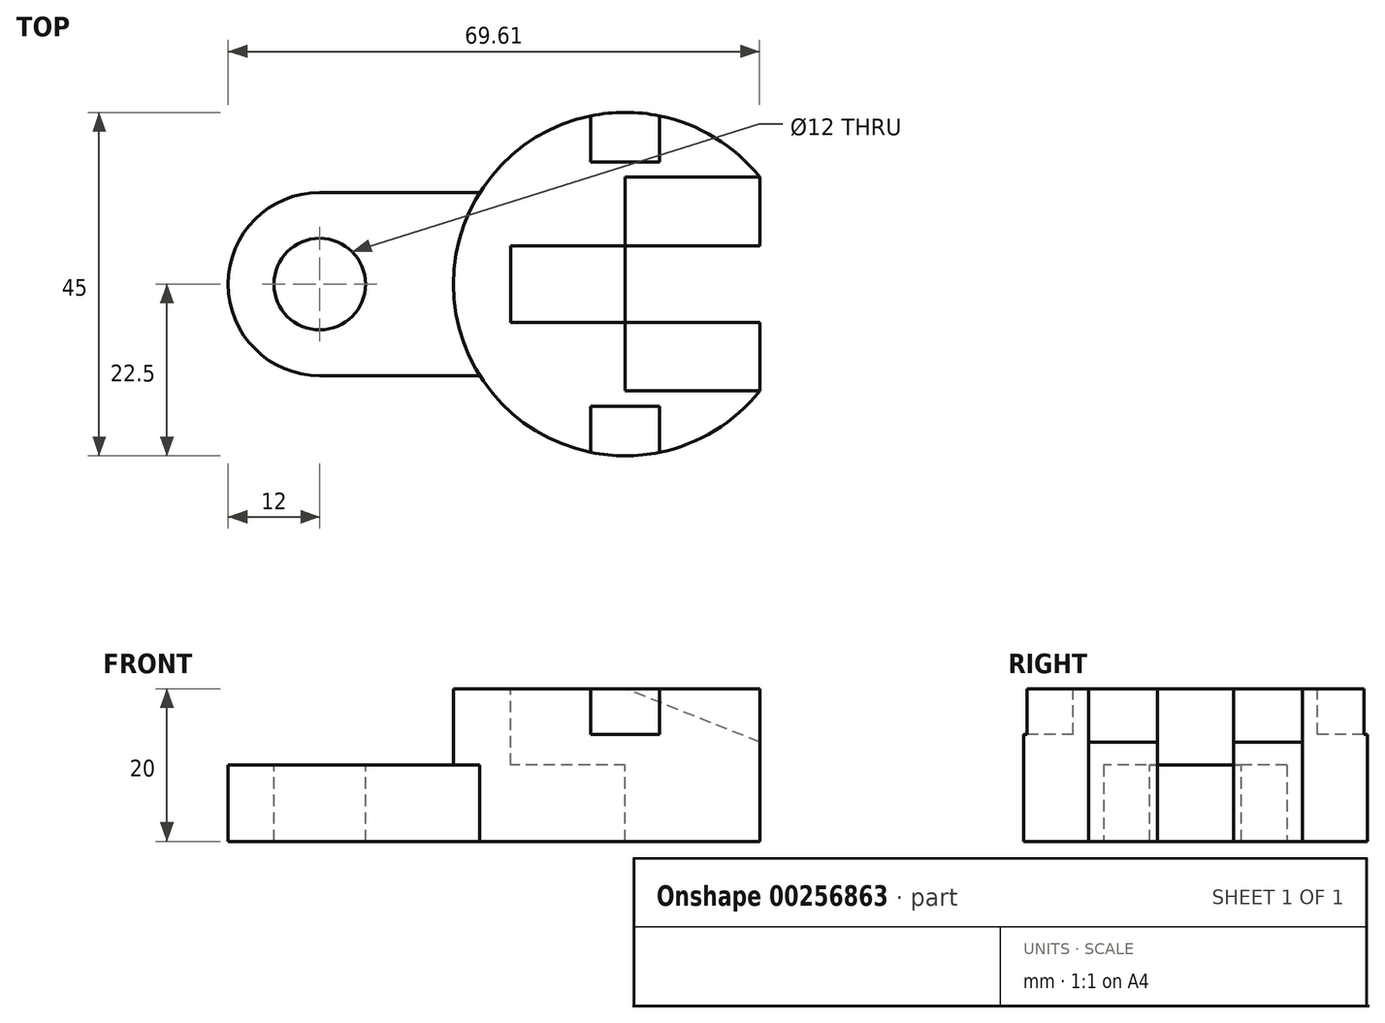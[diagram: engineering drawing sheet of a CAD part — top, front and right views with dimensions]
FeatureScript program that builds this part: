
annotation { "Feature Type Name" : "Feature", "Feature Type Description" : "" }
export const myFeature = defineFeature(function(context is Context, id is Id, definition is map)
    precondition{}
    {
        {
            var Q0;
            Q0=qCreatedBy(makeId("Top.planeOp"),FACE);
            var sketch = newSketch(context, id + "F0", { "sketchPlane" : qUnion([Q0])});
            skCircle(sketch, "E0", {"center": v(0, 0) * mm, "radius": 22.5 * mm});
            skSolve(sketch);
        }
        {
            var Q0;
            Q0=makeQuery(id+"F0.imprint","IMPRINT",FACE,{"disambiguationData":[TD([[makeQuery(id+"F0.imprint","IMPRINT",EDGE,{"derivedFrom":sQuery(id+"F0.wireOp",EDGE,"E0")}),1.0]])]});
            extrude(context, id + "F1", {"entities" : qUnion([Q0]), "endBound" : BoundingType.SYMMETRIC, "depth" : 20 * mm});
        }
        {
            var Q0;
            Q0=makeQuery(id+"F1.opExtrude","CAP_FACE",FACE,{"disambiguationData":[OSD([sQuery(id+"F0.wireOp",EDGE,"E0")])],"isStart":false});
            var sketch = newSketch(context, id + "F2", { "sketchPlane" : qUnion([Q0])});
            skLineSegment(sketch, "E1.bottom", {"start": v(22.5, -22.5) * mm, "end": v(-22.5, -22.5) * mm});
            skLineSegment(sketch, "E1.top", {"start": v(22.5, 22.5) * mm, "end": v(-22.5, 22.5) * mm});
            skLineSegment(sketch, "E1.left", {"start": v(22.5, -22.5) * mm, "end": v(22.5, 22.5) * mm});
            skLineSegment(sketch, "E1.right", {"start": v(-22.5, -22.5) * mm, "end": v(-22.5, 22.5) * mm});
            skPoint(sketch, "E1.middle", {"position": v(0, 0) * mm});
            skLineSegment(sketch, "E2", {"start": v(22.5, 14) * mm, "end": v(-22.5, 14) * mm});
            skLineSegment(sketch, "E3", {"start": v(22.5, -14) * mm, "end": v(-22.5, -14) * mm});
            skLineSegment(sketch, "E4", {"start": v(17.61, 14) * mm, "end": v(17.61, -14) * mm});
            skSolve(sketch);
        }
        {
            var Q0;
            {var subQ0=sQuery(id+"F2.wireOp",EDGE,"E4");Q0=makeQuery(id+"F2.imprint","IMPRINT",FACE,{"disambiguationData":[TD([[makeQuery(id+"F2.imprint","IMPRINT",EDGE,{"derivedFrom":subQ0}),1.0]])]});}
            extrude(context, id + "F3", {"entities" : qUnion([Q0]), "operationType" : NewBodyOperationType.REMOVE, "endBound" : BoundingType.THROUGH_ALL, "oppositeDirection" : true, "depth" : 25 * mm});
        }
        {
            var Q0;
            Q0=makeQuery(id+"F1.opExtrude","CAP_FACE",FACE,{"disambiguationData":[OSD([sQuery(id+"F0.wireOp",EDGE,"E0")])],"isStart":false});
            var sketch = newSketch(context, id + "F4", { "sketchPlane" : qUnion([Q0])});
            skLineSegment(sketch, "E5.bottom", {"start": v(22.5, 22.5) * mm, "end": v(-22.5, 22.5) * mm});
            skLineSegment(sketch, "E5.top", {"start": v(22.5, -22.5) * mm, "end": v(-22.5, -22.5) * mm});
            skLineSegment(sketch, "E5.left", {"start": v(22.5, 22.5) * mm, "end": v(22.5, -22.5) * mm});
            skLineSegment(sketch, "E5.right", {"start": v(-22.5, 22.5) * mm, "end": v(-22.5, -22.5) * mm});
            skPoint(sketch, "E5.middle", {"position": v(0, 0) * mm});
            skLineSegment(sketch, "E6", {"start": v(-22.5, 16) * mm, "end": v(22.5, 16) * mm});
            skLineSegment(sketch, "E7", {"start": v(-22.5, -16) * mm, "end": v(22.5, -16) * mm});
            skLineSegment(sketch, "E8", {"start": v(4.5, 22.05) * mm, "end": v(4.5, -22.05) * mm});
            skLineSegment(sketch, "E9", {"start": v(-4.5, 22.05) * mm, "end": v(-4.5, -22.05) * mm});
            skSolve(sketch);
        }
        {
            var Q0;
            {var subQ4=sQuery(id+"F4.wireOp",EDGE,"E9");var subQ6=sQuery(id+"F4.wireOp",EDGE,"E7");var subQ7=makeQuery(id+"F4.imprint","INTERSECT",VERTEX,{"derivedFrom":[subQ6,subQ4]});Q0=makeQuery(id+"F4.imprint","IMPRINT",FACE,{"disambiguationData":[TD([[makeQuery(id+"F4.imprint","IMPRINT",EDGE,{"disambiguationData":[TD([[subQ7,-1.0]])],"derivedFrom":subQ6}),-1.0]])]});}
            var Q1;
            {var subQ3=sQuery(id+"F4.wireOp",EDGE,"E6");var subQ6=sQuery(id+"F4.wireOp",EDGE,"E9");var subQ8=makeQuery(id+"F4.imprint","INTERSECT",VERTEX,{"derivedFrom":[subQ3,subQ6]});Q1=makeQuery(id+"F4.imprint","IMPRINT",FACE,{"disambiguationData":[TD([[makeQuery(id+"F4.imprint","IMPRINT",EDGE,{"disambiguationData":[TD([[subQ8,-1.0]])],"derivedFrom":subQ3}),1.0]])]});}
            extrude(context, id + "F5", {"entities" : qUnion([Q0, Q1]), "operationType" : NewBodyOperationType.REMOVE, "oppositeDirection" : true, "depth" : 6 * mm});
        }
        {
            var Q0;
            Q0=qCreatedBy(makeId("Front.planeOp"),FACE);
            var sketch = newSketch(context, id + "F6", { "sketchPlane" : qUnion([Q0])});
            skLineSegment(sketch, "E10.bottom", {"start": v(22.5, 10) * mm, "end": v(-22.5, 10) * mm});
            skLineSegment(sketch, "E10.top", {"start": v(22.5, -10) * mm, "end": v(-22.5, -10) * mm});
            skLineSegment(sketch, "E10.left", {"start": v(22.5, 10) * mm, "end": v(22.5, -10) * mm});
            skLineSegment(sketch, "E10.right", {"start": v(-22.5, 10) * mm, "end": v(-22.5, -10) * mm});
            skPoint(sketch, "E10.middle", {"position": v(0, 0) * mm});
            skLineSegment(sketch, "E11", {"start": v(-22.5, 3) * mm, "end": v(22.5, 3) * mm});
            skPoint(sketch, "E12.endSnap0", {"position": v(0, -10) * mm});
            skPoint(sketch, "E13", {"position": v(17.61, 3) * mm});
            skLineSegment(sketch, "E14", {"start": v(0, 10) * mm, "end": v(17.61, 3) * mm});
            skLineSegment(sketch, "E15", {"start": v(17.61, 3) * mm, "end": v(17.61, 10) * mm});
            skSolve(sketch);
        }
        {
            var Q0;
            {var subQ0=sQuery(id+"F6.wireOp",EDGE,"E14");Q0=makeQuery(id+"F6.imprint","IMPRINT",FACE,{"disambiguationData":[TD([[makeQuery(id+"F6.imprint","IMPRINT",EDGE,{"derivedFrom":subQ0}),1.0]])]});}
            extrude(context, id + "F7", {"entities" : qUnion([Q0]), "operationType" : NewBodyOperationType.REMOVE, "endBound" : BoundingType.SYMMETRIC, "oppositeDirection" : true, "depth" : 28 * mm});
        }
        {
            var Q0;
            Q0=qCreatedBy(makeId("Top.planeOp"),FACE);
            var sketch = newSketch(context, id + "F8", { "sketchPlane" : qUnion([Q0])});
            skLineSegment(sketch, "E16.bottom", {"start": v(22.5, 22.5) * mm, "end": v(-22.5, 22.5) * mm});
            skLineSegment(sketch, "E16.top", {"start": v(22.5, -22.5) * mm, "end": v(-22.5, -22.5) * mm});
            skLineSegment(sketch, "E16.left", {"start": v(22.5, 22.5) * mm, "end": v(22.5, -22.5) * mm});
            skLineSegment(sketch, "E16.right", {"start": v(-22.5, 22.5) * mm, "end": v(-22.5, -22.5) * mm});
            skPoint(sketch, "E16.middle", {"position": v(0, 0) * mm});
            skLineSegment(sketch, "E17", {"start": v(-22.5, 5) * mm, "end": v(22.5, 5) * mm});
            skLineSegment(sketch, "E18", {"start": v(-22.5, -5) * mm, "end": v(22.5, -5) * mm});
            skLineSegment(sketch, "E19", {"start": v(-15, 22.5) * mm, "end": v(-15, -22.5) * mm});
            skSolve(sketch);
        }
        {
            var Q0;
            {var subQ0=sQuery(id+"F8.wireOp",EDGE,"E17");var subQ1=sQuery(id+"F8.wireOp",EDGE,"E16.left");var subQ2=makeQuery(id+"F8.imprint","INTERSECT",VERTEX,{"derivedFrom":[subQ1,subQ0]});Q0=makeQuery(id+"F8.imprint","IMPRINT",FACE,{"disambiguationData":[TD([[makeQuery(id+"F8.imprint","IMPRINT",EDGE,{"disambiguationData":[TD([[subQ2,-1.0]])],"derivedFrom":subQ1}),-1.0]])]});}
            extrude(context, id + "F9", {"entities" : qUnion([Q0]), "operationType" : NewBodyOperationType.REMOVE, "endBound" : BoundingType.SYMMETRIC, "oppositeDirection" : true, "depth" : 20 * mm});
        }
        {
            var Q0;
            Q0=qCreatedBy(makeId("Right.planeOp"),FACE);
            var sketch = newSketch(context, id + "F10", { "sketchPlane" : qUnion([Q0])});
            skLineSegment(sketch, "E20.bottom", {"start": v(-22.5, 10) * mm, "end": v(22.5, 10) * mm});
            skLineSegment(sketch, "E20.top", {"start": v(-22.5, -10) * mm, "end": v(22.5, -10) * mm});
            skLineSegment(sketch, "E20.left", {"start": v(-22.5, 10) * mm, "end": v(-22.5, -10) * mm});
            skLineSegment(sketch, "E20.right", {"start": v(22.5, 10) * mm, "end": v(22.5, -10) * mm});
            skPoint(sketch, "E20.middle", {"position": v(0, 0) * mm});
            skLineSegment(sketch, "E21", {"start": v(12, 10) * mm, "end": v(12, -10) * mm});
            skLineSegment(sketch, "E22", {"start": v(-12, 10) * mm, "end": v(-12, -10) * mm});
            skLineSegment(sketch, "E23", {"start": v(22.5, 0) * mm, "end": v(-22.5, 0) * mm});
            skSolve(sketch);
        }
        {
            var Q0;
            {var subQ0=sQuery(id+"F10.wireOp",EDGE,"E21");var subQ1=sQuery(id+"F10.wireOp",EDGE,"E20.top");var subQ2=makeQuery(id+"F10.imprint","INTERSECT",VERTEX,{"derivedFrom":[subQ1,subQ0]});Q0=makeQuery(id+"F10.imprint","IMPRINT",FACE,{"disambiguationData":[TD([[makeQuery(id+"F10.imprint","IMPRINT",EDGE,{"disambiguationData":[TD([[subQ2,1.0]])],"derivedFrom":subQ1}),1.0]])]});}
            extrude(context, id + "F11", {"entities" : qUnion([Q0]), "operationType" : NewBodyOperationType.ADD, "oppositeDirection" : true, "depth" : 52 * mm});
        }
        {
            var Q0;
            Q0=qCreatedBy(makeId("Top.planeOp"),FACE);
            var sketch = newSketch(context, id + "F12", { "sketchPlane" : qUnion([Q0])});
            skLineSegment(sketch, "E24.bottom", {"start": v(-52, 22.5) * mm, "end": v(52, 22.5) * mm});
            skLineSegment(sketch, "E24.top", {"start": v(-52, -22.5) * mm, "end": v(52, -22.5) * mm});
            skLineSegment(sketch, "E24.left", {"start": v(-52, 22.5) * mm, "end": v(-52, -22.5) * mm});
            skLineSegment(sketch, "E24.right", {"start": v(52, 22.5) * mm, "end": v(52, -22.5) * mm});
            skPoint(sketch, "E24.middle", {"position": v(0, 0) * mm});
            skLineSegment(sketch, "E25", {"start": v(-40, -22.5) * mm, "end": v(-40, 22.5) * mm});
            skLineSegment(sketch, "E26", {"start": v(-52, -12) * mm, "end": v(52, -12) * mm});
            skLineSegment(sketch, "E27", {"start": v(-52, 12) * mm, "end": v(52, 12) * mm});
            skArc(sketch, "E28", {"start": v(-40, 12) * mm, "mid": v(-52, 0) * mm, "end": v(-40, -12) * mm});
            skSolve(sketch);
        }
        {
            var Q0;
            {var subQ0=sQuery(id+"F12.wireOp",EDGE,"E27");var subQ1=sQuery(id+"F12.wireOp",EDGE,"E24.left");var subQ2=makeQuery(id+"F12.imprint","INTERSECT",VERTEX,{"derivedFrom":[subQ1,subQ0]});Q0=makeQuery(id+"F12.imprint","IMPRINT",FACE,{"disambiguationData":[TD([[makeQuery(id+"F12.imprint","IMPRINT",EDGE,{"disambiguationData":[TD([[subQ2,-1.0]])],"derivedFrom":subQ1}),1.0]])]});}
            var Q1;
            {var subQ0=sQuery(id+"F12.wireOp",EDGE,"E26");var subQ1=sQuery(id+"F12.wireOp",EDGE,"E24.left");var subQ2=makeQuery(id+"F12.imprint","INTERSECT",VERTEX,{"derivedFrom":[subQ1,subQ0]});Q1=makeQuery(id+"F12.imprint","IMPRINT",FACE,{"disambiguationData":[TD([[makeQuery(id+"F12.imprint","IMPRINT",EDGE,{"disambiguationData":[TD([[subQ2,1.0]])],"derivedFrom":subQ1}),1.0]])]});}
            extrude(context, id + "F13", {"entities" : qUnion([Q0, Q1]), "operationType" : NewBodyOperationType.REMOVE, "oppositeDirection" : true, "depth" : 10 * mm});
        }
        {
            var Q0;
            Q0=sQuery(id+"F12.wireOp",VERTEX,"E28.center");
            var Q1;
            Q1=makeQuery(id+"F1.opExtrude","SWEPT_BODY",BODY,{"disambiguationData":[OSD([sQuery(id+"F0.wireOp",EDGE,"E0")])]});
            hole(context, id + "F14", {"style" : HoleStyle.SIMPLE, "endStyle" : HoleEndStyle.THROUGH, "holeDiameter" : 12 * mm, "tappedDepth" : 12 * mm, "tapClearance" : 3, "locations" : qUnion([Q0]), "scope" : qUnion([Q1])});
        }
    });
